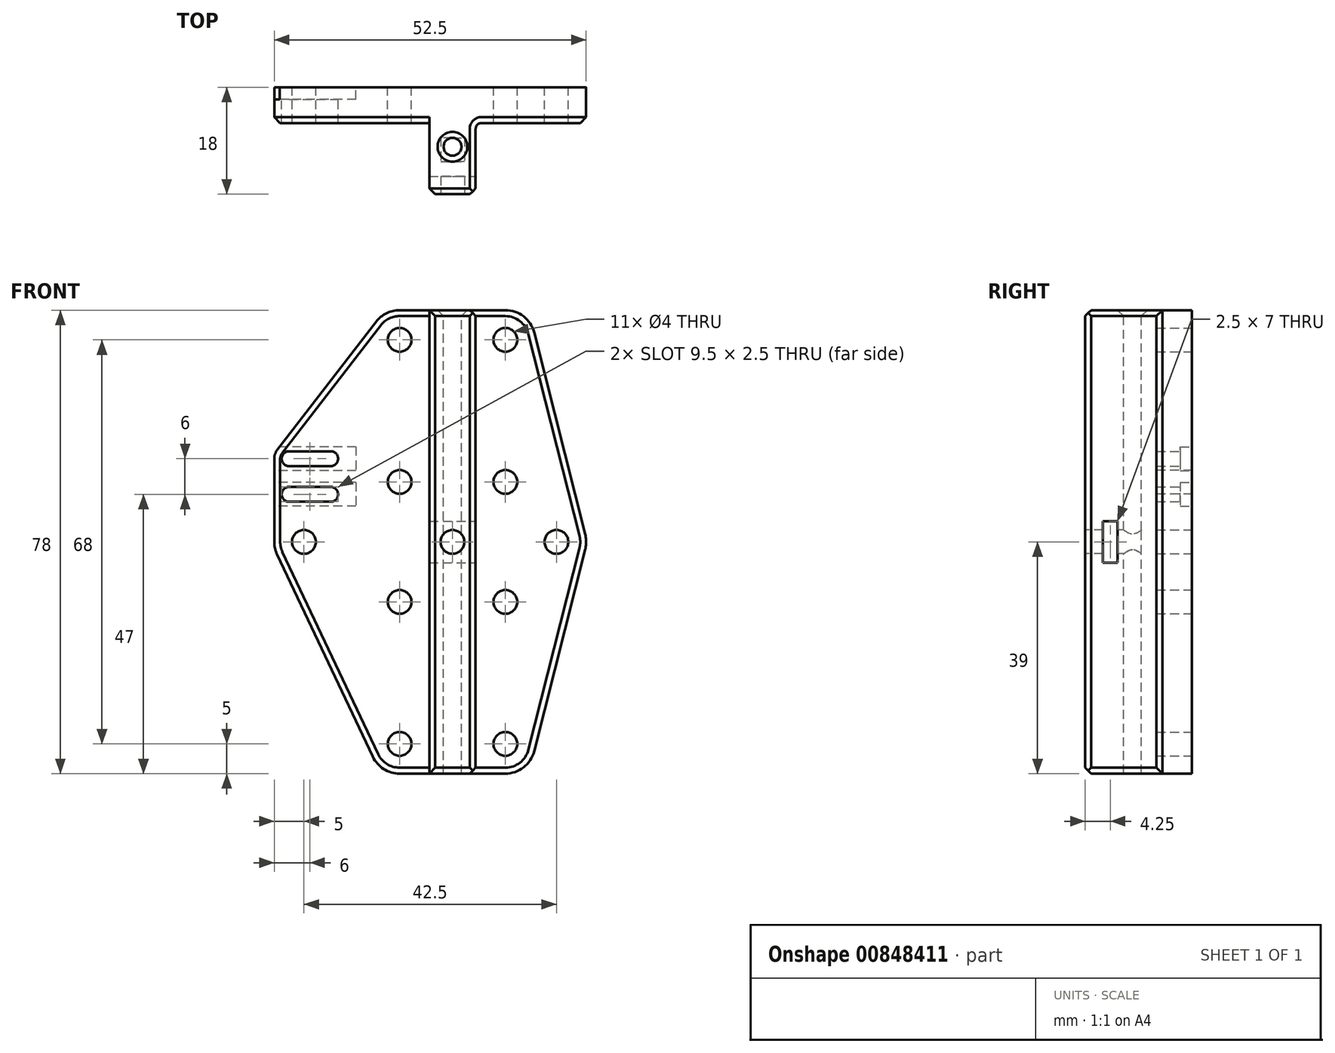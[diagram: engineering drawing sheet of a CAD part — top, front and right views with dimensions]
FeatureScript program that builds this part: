
annotation { "Feature Type Name" : "Feature", "Feature Type Description" : "" }
export const myFeature = defineFeature(function(context is Context, id is Id, definition is map)
    precondition{}
    {
        {
            var Q0;
            Q0=qCreatedBy(makeId("Front.planeOp"),FACE);
            var sketch = newSketch(context, id + "F0", { "sketchPlane" : qUnion([Q0])});
            skCircle(sketch, "E0", {"center": v(-25, 0) * mm, "radius": 2 * mm});
            skCircle(sketch, "E1", {"center": v(17.5, 0) * mm, "radius": 2 * mm});
            skCircle(sketch, "E2", {"center": v(8.9, 34) * mm, "radius": 2 * mm});
            skCircle(sketch, "E3", {"center": v(-8.9, -34) * mm, "radius": 2 * mm});
            skCircle(sketch, "E4", {"center": v(-8.9, 34) * mm, "radius": 2 * mm});
            skCircle(sketch, "E5", {"center": v(-8.9, 10.1) * mm, "radius": 2 * mm});
            skCircle(sketch, "E6", {"center": v(8.9, 10.1) * mm, "radius": 2 * mm});
            skCircle(sketch, "E7", {"center": v(-8.9, -10.1) * mm, "radius": 2 * mm});
            skCircle(sketch, "E8", {"center": v(8.9, -10.1) * mm, "radius": 2 * mm});
            skCircle(sketch, "E9", {"center": v(8.9, -34) * mm, "radius": 2 * mm});
            skArc(sketch, "E10", {"start": v(13.75, 35.23) * mm, "mid": v(11.97, 37.95) * mm, "end": v(8.9, 39) * mm});
            skArc(sketch, "E11", {"start": v(-8.9, 39) * mm, "mid": v(-11.1, 38.49) * mm, "end": v(-12.86, 37.06) * mm});
            skArc(sketch, "E12", {"start": v(-30, 0) * mm, "mid": v(-29.88, -1.1) * mm, "end": v(-29.52, -2.14) * mm});
            skArc(sketch, "E13", {"start": v(-13.42, -36.14) * mm, "mid": v(-11.57, -38.22) * mm, "end": v(-8.9, -39) * mm});
            skArc(sketch, "E14", {"start": v(8.9, -39) * mm, "mid": v(11.97, -37.95) * mm, "end": v(13.75, -35.23) * mm});
            skArc(sketch, "E15", {"start": v(22.35, -1.23) * mm, "mid": v(22.5, 0) * mm, "end": v(22.35, 1.23) * mm});
            skLineSegment(sketch, "E16", {"start": v(-29.52, -2.14) * mm, "end": v(-13.42, -36.14) * mm});
            skLineSegment(sketch, "E17", {"start": v(-8.9, -39) * mm, "end": v(8.9, -39) * mm});
            skLineSegment(sketch, "E18", {"start": v(13.75, -35.23) * mm, "end": v(22.35, -1.23) * mm});
            skLineSegment(sketch, "E19", {"start": v(22.35, 1.23) * mm, "end": v(13.75, 35.23) * mm});
            skLineSegment(sketch, "E20", {"start": v(8.9, 39) * mm, "end": v(-8.9, 39) * mm});
            skArc(sketch, "E21", {"start": v(-27.5, 15.25) * mm, "mid": v(-28.75, 14) * mm, "end": v(-27.5, 12.75) * mm});
            skArc(sketch, "E22", {"start": v(-20.5, 12.75) * mm, "mid": v(-19.25, 14) * mm, "end": v(-20.5, 15.25) * mm});
            skArc(sketch, "E23", {"start": v(-20.5, 6.75) * mm, "mid": v(-19.25, 8) * mm, "end": v(-20.5, 9.25) * mm});
            skArc(sketch, "E24", {"start": v(-27.5, 9.25) * mm, "mid": v(-28.75, 8) * mm, "end": v(-27.5, 6.75) * mm});
            skLineSegment(sketch, "E25", {"start": v(-27.5, 15.25) * mm, "end": v(-20.5, 15.25) * mm});
            skLineSegment(sketch, "E26", {"start": v(-27.5, 12.75) * mm, "end": v(-20.5, 12.75) * mm});
            skLineSegment(sketch, "E27", {"start": v(-20.5, 9.25) * mm, "end": v(-27.5, 9.25) * mm});
            skLineSegment(sketch, "E28", {"start": v(-27.5, 6.75) * mm, "end": v(-20.5, 6.75) * mm});
            skArc(sketch, "E29", {"start": v(-29.48, 15.53) * mm, "mid": v(-29.87, 14.8) * mm, "end": v(-30, 14) * mm});
            skLineSegment(sketch, "E30", {"start": v(-29.48, 15.53) * mm, "end": v(-12.86, 37.06) * mm});
            skLineSegment(sketch, "E31", {"start": v(-30, 14) * mm, "end": v(-30, 0) * mm});
            skSolve(sketch);
        }
        {
            var Q0;
            Q0=makeQuery(id+"F0.imprint","IMPRINT",FACE,{"disambiguationData":[TD([[makeQuery(id+"F0.imprint","IMPRINT",EDGE,{"derivedFrom":sQuery(id+"F0.wireOp",EDGE,"E0")}),-1.0]])]});
            extrude(context, id + "F1", {"entities" : qUnion([Q0]), "depth" : 6 * mm, "offsetDistance" : 25 * mm});
        }
        {
            var Q0;
            Q0=makeQuery(id+"F1.opExtrude","CAP_FACE",FACE,{"disambiguationData":[OSD([sQuery(id+"F0.wireOp",EDGE,"E0"),sQuery(id+"F0.wireOp",EDGE,"E1"),sQuery(id+"F0.wireOp",EDGE,"E2"),sQuery(id+"F0.wireOp",EDGE,"E3"),sQuery(id+"F0.wireOp",EDGE,"A7WbhDfQ-Xarm-HBb1-fWNh-Xkxg8LczOUE5"),sQuery(id+"F0.wireOp",EDGE,"PBMz9elX-7RSy-N3vm-Tmx0-kVTiYzk820eG"),sQuery(id+"F0.wireOp",EDGE,"OBzWWYXs-Zvwc-hS1g-dsdu-PxJbj0MhLyza"),sQuery(id+"F0.wireOp",EDGE,"iITc4q61-72gd-SqhD-kvq6-yIYcChUhvPZl"),sQuery(id+"F0.wireOp",EDGE,"Oz8ghYL7-ClGu-kczQ-QS9q-DKwblWpjAMmL"),sQuery(id+"F0.wireOp",EDGE,"Gttmuh1u-0Urr-uzdY-4qWh-yIlykMXOHso2"),sQuery(id+"F0.wireOp",EDGE,"G6OiUyu2-sFDx-HIP3-r46R-GbVrlVYmkgkI"),sQuery(id+"F0.wireOp",EDGE,"QfLxzBox-X6GG-Z3VP-jw9e-T8wXh8MqcLcg")])],"isStart":false});
            var sketch = newSketch(context, id + "F2", { "sketchPlane" : qUnion([Q0])});
            skCircle(sketch, "E32.0", {"center": v(-25, 0) * mm, "radius": 2 * mm});
            skCircle(sketch, "E33.0", {"center": v(-8.9, -34) * mm, "radius": 2 * mm});
            skCircle(sketch, "E34.0", {"center": v(17.5, 0) * mm, "radius": 2 * mm});
            skCircle(sketch, "E35.0", {"center": v(8.9, 34) * mm, "radius": 2 * mm});
            skLineSegment(sketch, "E36", {"start": v(-3.9, 39) * mm, "end": v(-3.9, -39) * mm});
            skLineSegment(sketch, "E37", {"start": v(3.9, -39) * mm, "end": v(3.9, 39) * mm});
            skPoint(sketch, "E38.0.7.end.orphan", {"position": v(-29.51, -2.16) * mm});
            skPoint(sketch, "E38.0.7.start.orphan", {"position": v(-28.55, 3.52) * mm});
            skPoint(sketch, "E38.0.1.start.orphan", {"position": v(-13.26, -36.16) * mm});
            skPoint(sketch, "E38.0.3.end.orphan", {"position": v(22.34, 1.25) * mm});
            skPoint(sketch, "E38.0.3.start.orphan", {"position": v(27.76, -7.92) * mm});
            skPoint(sketch, "E38.0.5.start.orphan", {"position": v(13.6, 35.25) * mm});
            skPoint(sketch, "E39.orphan", {"position": v(5.2, 37.52) * mm});
            skLineSegment(sketch, "E40", {"start": v(-3.9, 39) * mm, "end": v(3.9, 39) * mm});
            skLineSegment(sketch, "E41", {"start": v(3.9, -39) * mm, "end": v(-3.9, -39) * mm});
            skSolve(sketch);
        }
        {
            var Q0;
            Q0=makeQuery(id+"F2.imprint","IMPRINT",FACE,{"disambiguationData":[TD([[makeQuery(id+"F2.imprint","IMPRINT",EDGE,{"derivedFrom":sQuery(id+"F2.wireOp",EDGE,"E36")}),1.0]])]});
            extrude(context, id + "F3", {"entities" : qUnion([Q0]), "operationType" : NewBodyOperationType.ADD, "depth" : 12 * mm, "offsetDistance" : 25 * mm});
        }
        {
            var Q0;
            Q0=makeQuery(id+"F3.opExtrude","CAP_FACE",FACE,{"disambiguationData":[OSD([sQuery(id+"F2.wireOp",EDGE,"E36"),sQuery(id+"F2.wireOp",EDGE,"E37"),sQuery(id+"F2.wireOp",EDGE,"7ShLnBwf-IVbI-IhpM-fJta-Kkbz9xF4ikTS"),sQuery(id+"F2.wireOp",EDGE,"VPm3y5CP-oXX8-yRWZ-Vef4-mlM2h5b3Jh5a")])],"isStart":false});
            var sketch = newSketch(context, id + "F4", { "sketchPlane" : qUnion([Q0])});
            skCircle(sketch, "E42", {"center": v(0, 0) * mm, "radius": 2 * mm});
            skSolve(sketch);
        }
        {
            var Q0;
            Q0=makeQuery(id+"F4.imprint","IMPRINT",FACE,{"disambiguationData":[TD([[makeQuery(id+"F4.imprint","IMPRINT",EDGE,{"derivedFrom":sQuery(id+"F4.wireOp",EDGE,"E42")}),1.0]])]});
            var Q1;
            {var subQ0=sQuery(id+"F0.wireOp",EDGE,"iITc4q61-72gd-SqhD-kvq6-yIYcChUhvPZl");var subQ1=sQuery(id+"F0.wireOp",EDGE,"OBzWWYXs-Zvwc-hS1g-dsdu-PxJbj0MhLyza");var subQ2=sQuery(id+"F0.wireOp",EDGE,"E3");var subQ3=sQuery(id+"F0.wireOp",EDGE,"E0");var subQ4=sQuery(id+"F0.wireOp",EDGE,"Gttmuh1u-0Urr-uzdY-4qWh-yIlykMXOHso2");var subQ5=sQuery(id+"F0.wireOp",EDGE,"Oz8ghYL7-ClGu-kczQ-QS9q-DKwblWpjAMmL");var subQ6=sQuery(id+"F0.wireOp",EDGE,"QfLxzBox-X6GG-Z3VP-jw9e-T8wXh8MqcLcg");Q1=makeQuery(id+"F3.boolean.opBoolean","SPLIT",FACE,{"disambiguationData":[TD([makeQuery(id+"F1.opExtrude","SWEPT_FACE",FACE,{"disambiguationData":[OSD([subQ3])]})])],"derivedFrom":makeQuery(id+"F1.opExtrude","CAP_FACE",FACE,{"disambiguationData":[OSD([subQ3,sQuery(id+"F0.wireOp",EDGE,"E1"),sQuery(id+"F0.wireOp",EDGE,"E2"),subQ2,sQuery(id+"F0.wireOp",EDGE,"A7WbhDfQ-Xarm-HBb1-fWNh-Xkxg8LczOUE5"),sQuery(id+"F0.wireOp",EDGE,"PBMz9elX-7RSy-N3vm-Tmx0-kVTiYzk820eG"),subQ1,subQ0,subQ5,subQ4,sQuery(id+"F0.wireOp",EDGE,"G6OiUyu2-sFDx-HIP3-r46R-GbVrlVYmkgkI"),subQ6])],"isStart":false})});}
            extrude(context, id + "F5", {"entities" : qUnion([Q0]), "operationType" : NewBodyOperationType.REMOVE, "endBound" : BoundingType.UP_TO_SURFACE, "oppositeDirection" : true, "depth" : 25 * mm, "endBoundEntityFace" : qUnion([Q1]), "offsetDistance" : 25 * mm});
        }
        {
            var Q0;
            Q0=makeQuery(id+"F3.opExtrude","SWEPT_FACE",FACE,{"disambiguationData":[OSD([sQuery(id+"F2.wireOp",EDGE,"E37")])]});
            var sketch = newSketch(context, id + "F6", { "sketchPlane" : qUnion([Q0])});
            skLineSegment(sketch, "E43.bottom", {"start": v(-15, 3.5) * mm, "end": v(-12.5, 3.5) * mm});
            skLineSegment(sketch, "E43.top", {"start": v(-15, -3.5) * mm, "end": v(-12.5, -3.5) * mm});
            skLineSegment(sketch, "E43.left", {"start": v(-15, 3.5) * mm, "end": v(-15, -3.5) * mm});
            skLineSegment(sketch, "E43.right", {"start": v(-12.5, 3.5) * mm, "end": v(-12.5, -3.5) * mm});
            skPoint(sketch, "E44", {"position": v(-15, 0) * mm});
            skPoint(sketch, "E45", {"position": v(-13, 0) * mm});
            skSolve(sketch);
        }
        {
            var Q0;
            {var subQ0=sQuery(id+"F6.wireOp",EDGE,"CICxmz5F-YeQS-G6Q6-vbbA-lfoclgCKDJSC");Q0=makeQuery(id+"F6.imprint","IMPRINT",FACE,{"disambiguationData":[TD([[makeQuery(id+"F6.imprint","IMPRINT",EDGE,{"derivedFrom":subQ0}),1.0]])]});}
            var Q1;
            {var subQ0=sQuery(id+"F6.wireOp",EDGE,"E43.bottom");Q1=makeQuery(id+"F6.imprint","IMPRINT",FACE,{"disambiguationData":[TD([[makeQuery(id+"F6.imprint","IMPRINT",EDGE,{"derivedFrom":subQ0}),-1.0]])]});}
            extrude(context, id + "F7", {"entities" : qUnion([Q0, Q1]), "operationType" : NewBodyOperationType.REMOVE, "endBound" : BoundingType.THROUGH_ALL, "oppositeDirection" : true, "depth" : 25 * mm, "offsetDistance" : 25 * mm});
        }
        {
            var Q0;
            Q0=qCreatedBy(makeId("Top.planeOp"),FACE);
            var sketch = newSketch(context, id + "F8", { "sketchPlane" : qUnion([Q0])});
            skCircle(sketch, "E46", {"center": v(0, -10) * mm, "radius": 1.5 * mm});
            skSolve(sketch);
        }
        {
            var Q0;
            Q0=makeQuery(id+"F8.imprint","IMPRINT",FACE,{"disambiguationData":[TD([[makeQuery(id+"F8.imprint","IMPRINT",EDGE,{"derivedFrom":sQuery(id+"F8.wireOp",EDGE,"E46")}),1.0]])]});
            extrude(context, id + "F9", {"entities" : qUnion([Q0]), "operationType" : NewBodyOperationType.REMOVE, "endBound" : BoundingType.THROUGH_ALL, "oppositeDirection" : true, "depth" : 25 * mm, "offsetDistance" : 25 * mm, "hasSecondDirection" : true, "secondDirectionBound" : SecondDirectionBoundingType.THROUGH_ALL, "secondDirectionOppositeDirection" : false, "secondDirectionDepth" : 25 * mm});
        }
        {
            var Q0;
            Q0=makeQuery(id+"F5.boolean.opBoolean","COPY",FACE,{"derivedFrom":makeQuery(id+"F5.opExtrude","CAP_FACE",FACE,{"disambiguationData":[OSD([sQuery(id+"F4.wireOp",EDGE,"E42")])],"isStart":false})});
            extrude(context, id + "F10", {"entities" : qUnion([Q0]), "operationType" : NewBodyOperationType.ADD, "depth" : 2.5 * mm, "offsetDistance" : 25 * mm});
        }
        {
            var Q0;
            Q0=makeQuery(id+"F3.opExtrude","CAP_EDGE",EDGE,{"disambiguationData":[OSD([sQuery(id+"F2.wireOp",EDGE,"E37")])],"isStart":false});
            var Q1;
            Q1=makeQuery(id+"F3.opExtrude","CAP_EDGE",EDGE,{"disambiguationData":[OSD([sQuery(id+"F2.wireOp",EDGE,"E36")])],"isStart":false});
            chamfer(context, id + "F11", {"entities" : qUnion([Q0, Q1]), "width" : 1 * mm, "tangentPropagation" : true});
        }
        {
            var Q0;
            Q0=makeQuery(id+"F3.opExtrude","CAP_EDGE",EDGE,{"disambiguationData":[OSD([sQuery(id+"F2.wireOp",EDGE,"E36")])],"isStart":true});
            var Q1;
            Q1=makeQuery(id+"F3.opExtrude","CAP_EDGE",EDGE,{"disambiguationData":[OSD([sQuery(id+"F2.wireOp",EDGE,"E37")])],"isStart":true});
            fillet(context, id + "F12", {"entities" : qUnion([Q0, Q1]), "radius" : 1 * mm, "tangentPropagation" : true, "allowEdgeOverflow" : false});
        }
        {
            var Q0;
            Q0=makeQuery(id+"F1.opExtrude","CAP_EDGE",EDGE,{"disambiguationData":[OSD([sQuery(id+"F0.wireOp",EDGE,"s2vCef00-h9bP-xnIe-qE8i-07BUZpMs55S6")])],"isStart":false});
            var Q1;
            Q1=makeQuery(id+"F1.opExtrude","CAP_EDGE",EDGE,{"disambiguationData":[OSD([sQuery(id+"F0.wireOp",EDGE,"E19")])],"isStart":false});
            var Q2;
            Q2=makeQuery(id+"F3.opExtrude","CAP_EDGE",EDGE,{"disambiguationData":[OSD([sQuery(id+"F2.wireOp",EDGE,"E41")])],"isStart":false});
            var Q3;
            Q3=makeQuery(id+"F3.opExtrude","CAP_EDGE",EDGE,{"disambiguationData":[OSD([sQuery(id+"F2.wireOp",EDGE,"E40")])],"isStart":false});
            var Q4;
            Q4=makeQuery(id+"F1.opExtrude","CAP_EDGE",EDGE,{"disambiguationData":[OSD([sQuery(id+"F0.wireOp",EDGE,"E31")])],"isStart":false});
            chamfer(context, id + "F13", {"entities" : qUnion([Q0, Q1, Q2, Q3, Q4]), "width" : 1 * mm, "tangentPropagation" : true});
        }
        {
            var Q0;
            Q0=makeQuery(id+"F9.boolean.opBoolean","INTERSECT",EDGE,{"derivedFrom":[makeQuery(id+"F3.boolean.opBoolean","MERGE",FACE,{"derivedFrom":[makeQuery(id+"F1.opExtrude","SWEPT_FACE",FACE,{"disambiguationData":[OSD([sQuery(id+"F0.wireOp",EDGE,"E20")])]}),makeQuery(id+"F3.opExtrude","SWEPT_FACE",FACE,{"disambiguationData":[OSD([sQuery(id+"F2.wireOp",EDGE,"E40")])]})]}),makeQuery(id+"F9.opExtrude","SWEPT_FACE",FACE,{"disambiguationData":[OSD([sQuery(id+"F8.wireOp",EDGE,"E46")])]})]});
            chamfer(context, id + "F14", {"entities" : qUnion([Q0]), "width" : 1 * mm, "tangentPropagation" : true});
        }
        {
            var Q0;
            Q0=makeQuery(id+"F1.opExtrude","CAP_FACE",FACE,{"disambiguationData":[OSD([sQuery(id+"F0.wireOp",EDGE,"E0"),sQuery(id+"F0.wireOp",EDGE,"E1"),sQuery(id+"F0.wireOp",EDGE,"E2"),sQuery(id+"F0.wireOp",EDGE,"E3"),sQuery(id+"F0.wireOp",EDGE,"E4"),sQuery(id+"F0.wireOp",EDGE,"E5"),sQuery(id+"F0.wireOp",EDGE,"E6"),sQuery(id+"F0.wireOp",EDGE,"E7"),sQuery(id+"F0.wireOp",EDGE,"E8"),sQuery(id+"F0.wireOp",EDGE,"E9"),sQuery(id+"F0.wireOp",EDGE,"E10"),sQuery(id+"F0.wireOp",EDGE,"E11"),sQuery(id+"F0.wireOp",EDGE,"E12"),sQuery(id+"F0.wireOp",EDGE,"E13"),sQuery(id+"F0.wireOp",EDGE,"E14"),sQuery(id+"F0.wireOp",EDGE,"E15"),sQuery(id+"F0.wireOp",EDGE,"E16"),sQuery(id+"F0.wireOp",EDGE,"E17"),sQuery(id+"F0.wireOp",EDGE,"E18"),sQuery(id+"F0.wireOp",EDGE,"E19"),sQuery(id+"F0.wireOp",EDGE,"E20"),sQuery(id+"F0.wireOp",EDGE,"E21"),sQuery(id+"F0.wireOp",EDGE,"E22"),sQuery(id+"F0.wireOp",EDGE,"E23"),sQuery(id+"F0.wireOp",EDGE,"E24"),sQuery(id+"F0.wireOp",EDGE,"E25"),sQuery(id+"F0.wireOp",EDGE,"E26"),sQuery(id+"F0.wireOp",EDGE,"E27"),sQuery(id+"F0.wireOp",EDGE,"E28"),sQuery(id+"F0.wireOp",EDGE,"E29"),sQuery(id+"F0.wireOp",EDGE,"E30"),sQuery(id+"F0.wireOp",EDGE,"E31")])],"isStart":true});
            var sketch = newSketch(context, id + "F15", { "sketchPlane" : qUnion([Q0])});
            skLineSegment(sketch, "E47.bottom", {"start": v(16.25, 16) * mm, "end": v(31.25, 16) * mm});
            skLineSegment(sketch, "E47.top", {"start": v(16.25, 12) * mm, "end": v(31.25, 12) * mm});
            skLineSegment(sketch, "E47.left", {"start": v(16.25, 16) * mm, "end": v(16.25, 12) * mm});
            skLineSegment(sketch, "E47.right", {"start": v(31.25, 16) * mm, "end": v(31.25, 12) * mm});
            skLineSegment(sketch, "E48.bottom", {"start": v(16.25, 10) * mm, "end": v(31.25, 10) * mm});
            skLineSegment(sketch, "E48.top", {"start": v(16.25, 6) * mm, "end": v(31.25, 6) * mm});
            skLineSegment(sketch, "E48.left", {"start": v(16.25, 10) * mm, "end": v(16.25, 6) * mm});
            skLineSegment(sketch, "E48.right", {"start": v(31.25, 10) * mm, "end": v(31.25, 6) * mm});
            skArc(sketch, "E49.0.0", {"start": v(29.52, -2.14) * mm, "mid": v(29.88, -1.1) * mm, "end": v(30, 0) * mm});
            skLineSegment(sketch, "E49.0.1", {"start": v(30, 0) * mm, "end": v(30, 14) * mm});
            skArc(sketch, "E49.0.2", {"start": v(30, 14) * mm, "mid": v(29.87, 14.8) * mm, "end": v(29.48, 15.53) * mm});
            skLineSegment(sketch, "E49.0.3", {"start": v(29.48, 15.53) * mm, "end": v(12.86, 37.06) * mm});
            skArc(sketch, "E49.0.4", {"start": v(12.86, 37.06) * mm, "mid": v(11.1, 38.49) * mm, "end": v(8.9, 39) * mm});
            skLineSegment(sketch, "E49.0.5", {"start": v(8.9, 39) * mm, "end": v(-8.9, 39) * mm});
            skArc(sketch, "E49.0.6", {"start": v(-8.9, 39) * mm, "mid": v(-11.97, 37.95) * mm, "end": v(-13.75, 35.23) * mm});
            skLineSegment(sketch, "E49.0.7", {"start": v(-13.75, 35.23) * mm, "end": v(-22.35, 1.23) * mm});
            skArc(sketch, "E49.0.8", {"start": v(-22.35, 1.23) * mm, "mid": v(-22.5, 0) * mm, "end": v(-22.35, -1.23) * mm});
            skLineSegment(sketch, "E49.0.9", {"start": v(-22.35, -1.23) * mm, "end": v(-13.75, -35.23) * mm});
            skArc(sketch, "E49.0.10", {"start": v(-13.75, -35.23) * mm, "mid": v(-11.97, -37.95) * mm, "end": v(-8.9, -39) * mm});
            skLineSegment(sketch, "E49.0.11", {"start": v(-8.9, -39) * mm, "end": v(8.9, -39) * mm});
            skArc(sketch, "E49.0.12", {"start": v(8.9, -39) * mm, "mid": v(11.57, -38.22) * mm, "end": v(13.42, -36.14) * mm});
            skLineSegment(sketch, "E49.0.13", {"start": v(13.42, -36.14) * mm, "end": v(29.52, -2.14) * mm});
            skPoint(sketch, "E50", {"position": v(16.25, 14) * mm});
            skPoint(sketch, "E51", {"position": v(16.25, 8) * mm});
            skPoint(sketch, "E52", {"position": v(27.5, 8) * mm});
            skSolve(sketch);
        }
        {
            var Q0;
            {var subQ4=sQuery(id+"F15.wireOp",EDGE,"E47.left");Q0=makeQuery(id+"F15.imprint","IMPRINT",FACE,{"disambiguationData":[TD([[makeQuery(id+"F15.imprint","IMPRINT",EDGE,{"derivedFrom":subQ4}),1.0]])]});}
            var Q1;
            {var subQ5=sQuery(id+"F15.wireOp",EDGE,"E48.left");Q1=makeQuery(id+"F15.imprint","IMPRINT",FACE,{"disambiguationData":[TD([[makeQuery(id+"F15.imprint","IMPRINT",EDGE,{"derivedFrom":subQ5}),1.0]])]});}
            extrude(context, id + "F16", {"entities" : qUnion([Q0, Q1]), "operationType" : NewBodyOperationType.REMOVE, "oppositeDirection" : true, "depth" : 2 * mm, "offsetDistance" : 25 * mm});
        }
    });
